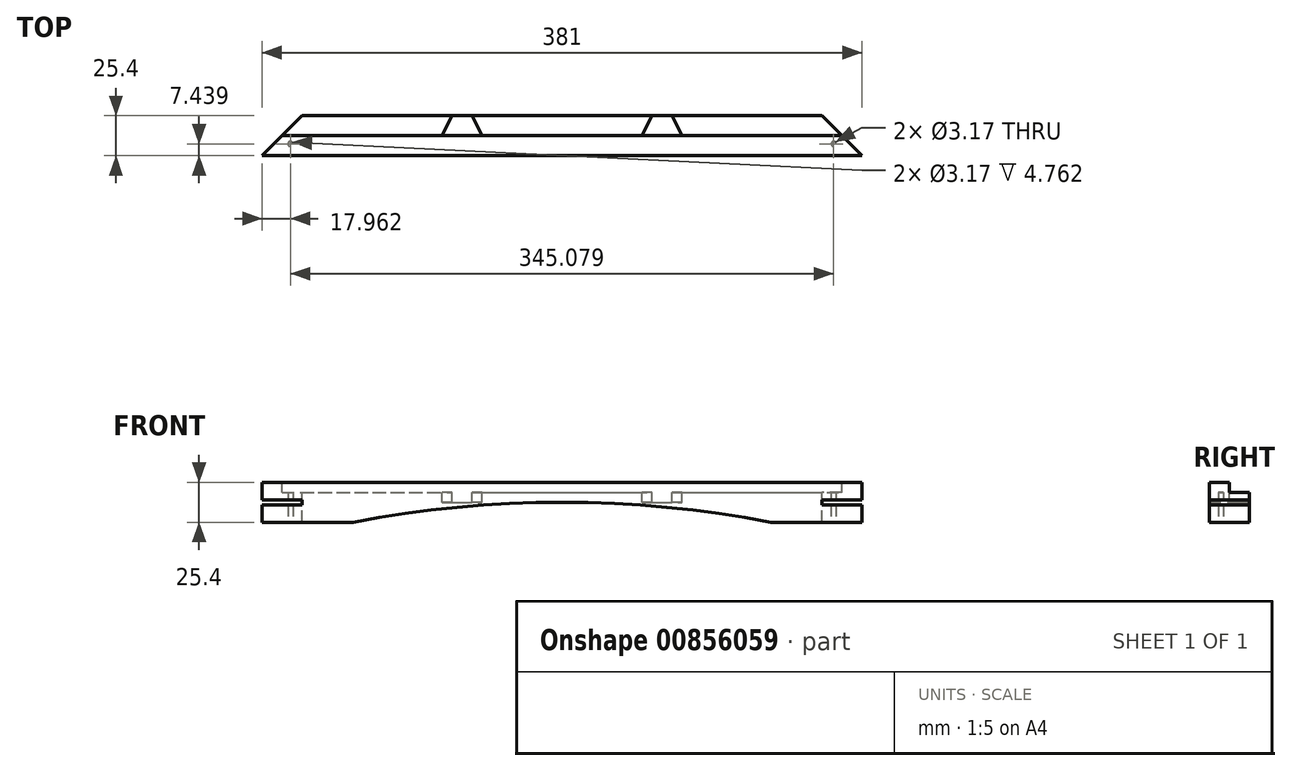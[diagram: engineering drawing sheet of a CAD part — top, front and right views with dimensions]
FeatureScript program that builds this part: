
annotation { "Feature Type Name" : "Feature", "Feature Type Description" : "" }
export const myFeature = defineFeature(function(context is Context, id is Id, definition is map)
    precondition{}
    {
        {
            var Q0;
            Q0=qCreatedBy(makeId("Front.planeOp"),FACE);
            var sketch = newSketch(context, id + "F0", { "sketchPlane" : qUnion([Q0])});
            skLineSegment(sketch, "E0.bottom", {"start": v(-134.34, 12.7) * mm, "end": v(246.66, 12.7) * mm});
            skLineSegment(sketch, "E0.top", {"start": v(-134.34, -12.7) * mm, "end": v(246.66, -12.7) * mm});
            skLineSegment(sketch, "E0.left", {"start": v(-134.34, 12.7) * mm, "end": v(-134.34, -12.7) * mm});
            skLineSegment(sketch, "E0.right", {"start": v(246.66, 12.7) * mm, "end": v(246.66, -12.7) * mm});
            skCircle(sketch, "E1", {"center": v(56.16, -698.5) * mm, "radius": 698.5 * mm});
            skLineSegment(sketch, "E2", {"start": v(-70.84, -12.7) * mm, "end": v(81.85, -12.7) * mm});
            skSolve(sketch);
        }
        {
            var Q0;
            Q0=makeQuery(id+"F0.imprint","IMPRINT",FACE,{"disambiguationData":[TD([[makeQuery(id+"F0.imprint","IMPRINT",EDGE,{"derivedFrom":sQuery(id+"F0.wireOp",EDGE,"E0.bottom")}),-1.0]])]});
            extrude(context, id + "F1", {"entities" : qUnion([Q0]), "depth" : 25.4 * mm, "offsetDistance" : 25.4 * mm});
        }
        {
            var Q0;
            Q0=makeQuery(id+"F1.opExtrude","SWEPT_FACE",FACE,{"disambiguationData":[OSD([sQuery(id+"F0.wireOp",EDGE,"E0.right")])]});
            var sketch = newSketch(context, id + "F2", { "sketchPlane" : qUnion([Q0])});
            skLineSegment(sketch, "E3.bottom", {"start": v(-25.4, 1.59) * mm, "end": v(0, 1.59) * mm});
            skLineSegment(sketch, "E3.top", {"start": v(-25.4, -1.59) * mm, "end": v(0, -1.59) * mm});
            skLineSegment(sketch, "E3.left", {"start": v(-25.4, 1.59) * mm, "end": v(-25.4, -1.59) * mm});
            skLineSegment(sketch, "E3.right", {"start": v(0, 1.59) * mm, "end": v(0, -1.59) * mm});
            skSolve(sketch);
        }
        {
            var Q0;
            Q0=makeQuery(id+"F2.imprint","IMPRINT",FACE,{"disambiguationData":[TD([[makeQuery(id+"F2.imprint","IMPRINT",EDGE,{"derivedFrom":sQuery(id+"F2.wireOp",EDGE,"E3.bottom")}),-1.0]])]});
            extrude(context, id + "F3", {"entities" : qUnion([Q0]), "operationType" : NewBodyOperationType.REMOVE, "oppositeDirection" : true, "depth" : 25.4 * mm, "offsetDistance" : 25.4 * mm});
        }
        {
            var Q0;
            Q0=makeQuery(id+"F1.opExtrude","SWEPT_FACE",FACE,{"disambiguationData":[OSD([sQuery(id+"F0.wireOp",EDGE,"E0.left")])]});
            var sketch = newSketch(context, id + "F4", { "sketchPlane" : qUnion([Q0])});
            skLineSegment(sketch, "E4.bottom", {"start": v(0, 1.59) * mm, "end": v(25.4, 1.59) * mm});
            skLineSegment(sketch, "E4.top", {"start": v(0, -1.59) * mm, "end": v(25.4, -1.59) * mm});
            skLineSegment(sketch, "E4.left", {"start": v(0, 1.59) * mm, "end": v(0, -1.59) * mm});
            skLineSegment(sketch, "E4.right", {"start": v(25.4, 1.59) * mm, "end": v(25.4, -1.59) * mm});
            skSolve(sketch);
        }
        {
            var Q0;
            Q0=makeQuery(id+"F4.imprint","IMPRINT",FACE,{"disambiguationData":[TD([[makeQuery(id+"F4.imprint","IMPRINT",EDGE,{"derivedFrom":sQuery(id+"F4.wireOp",EDGE,"E4.bottom")}),-1.0]])]});
            extrude(context, id + "F5", {"entities" : qUnion([Q0]), "operationType" : NewBodyOperationType.REMOVE, "oppositeDirection" : true, "depth" : 25.4 * mm, "offsetDistance" : 25.4 * mm});
        }
        {
            var Q0;
            Q0=makeQuery(id+"F1.opExtrude","SWEPT_FACE",FACE,{"disambiguationData":[OSD([sQuery(id+"F0.wireOp",EDGE,"E0.bottom")])]});
            var sketch = newSketch(context, id + "F6", { "sketchPlane" : qUnion([Q0])});
            skLineSegment(sketch, "E5", {"start": v(-134.34, -25.4) * mm, "end": v(-108.94, 0) * mm});
            skLineSegment(sketch, "E6", {"start": v(246.66, -25.4) * mm, "end": v(221.26, 0) * mm});
            skLineSegment(sketch, "E7", {"start": v(-121.64, -12.7) * mm, "end": v(233.96, -12.7) * mm});
            skSolve(sketch);
        }
        {
            var Q0;
            {var subQ0=sQuery(id+"F6.wireOp",EDGE,"E5");Q0=makeQuery(id+"F6.imprint","IMPRINT",FACE,{"disambiguationData":[TD([[makeQuery(id+"F6.imprint","IMPRINT",EDGE,{"derivedFrom":subQ0}),1.0]])]});}
            var Q1;
            {var subQ0=sQuery(id+"F6.wireOp",EDGE,"E6");Q1=makeQuery(id+"F6.imprint","IMPRINT",FACE,{"disambiguationData":[TD([[makeQuery(id+"F6.imprint","IMPRINT",EDGE,{"derivedFrom":subQ0}),-1.0]])]});}
            extrude(context, id + "F7", {"entities" : qUnion([Q0, Q1]), "operationType" : NewBodyOperationType.REMOVE, "oppositeDirection" : true, "depth" : 25.4 * mm, "offsetDistance" : 25.4 * mm});
        }
        {
            var Q0;
            {var subQ3=sQuery(id+"F6.wireOp",EDGE,"E7");Q0=makeQuery(id+"F6.imprint","IMPRINT",FACE,{"disambiguationData":[TD([[makeQuery(id+"F6.imprint","IMPRINT",EDGE,{"derivedFrom":subQ3}),1.0]])]});}
            extrude(context, id + "F8", {"entities" : qUnion([Q0]), "operationType" : NewBodyOperationType.REMOVE, "oppositeDirection" : true, "depth" : 6.35 * mm, "offsetDistance" : 25.4 * mm});
        }
        {
            var Q0;
            Q0=makeQuery(id+"F8.boolean.opBoolean","COPY",FACE,{"derivedFrom":makeQuery(id+"F8.opExtrude","CAP_FACE",FACE,{"disambiguationData":[OSD([sQuery(id+"F0.wireOp",EDGE,"E0.bottom"),sQuery(id+"F6.wireOp",EDGE,"E5"),sQuery(id+"F6.wireOp",EDGE,"E6"),sQuery(id+"F6.wireOp",EDGE,"E7")])],"isStart":false})});
            var sketch = newSketch(context, id + "F9", { "sketchPlane" : qUnion([Q0])});
            skLineSegment(sketch, "E8", {"start": v(-13.69, 0) * mm, "end": v(-20.04, -12.7) * mm});
            skLineSegment(sketch, "E9", {"start": v(-20.04, -12.7) * mm, "end": v(5.36, -12.7) * mm});
            skLineSegment(sketch, "E10", {"start": v(5.36, -12.7) * mm, "end": v(-0.99, 0) * mm});
            skLineSegment(sketch, "E11", {"start": v(113.31, 0) * mm, "end": v(106.96, -12.7) * mm});
            skLineSegment(sketch, "E12", {"start": v(106.96, -12.7) * mm, "end": v(132.36, -12.7) * mm});
            skLineSegment(sketch, "E13", {"start": v(132.36, -12.7) * mm, "end": v(126.01, 0) * mm});
            skLineSegment(sketch, "E14", {"start": v(-121.64, -12.7) * mm, "end": v(-20.04, -12.7) * mm});
            skLineSegment(sketch, "E15", {"start": v(5.36, -12.7) * mm, "end": v(106.96, -12.7) * mm});
            skLineSegment(sketch, "E16", {"start": v(132.36, -12.7) * mm, "end": v(233.96, -12.7) * mm});
            skLineSegment(sketch, "E17", {"start": v(-13.69, 0) * mm, "end": v(-108.94, 0) * mm});
            skLineSegment(sketch, "E18", {"start": v(-0.99, 0) * mm, "end": v(113.31, 0) * mm});
            skLineSegment(sketch, "E19", {"start": v(126.01, 0) * mm, "end": v(221.26, 0) * mm});
            skSolve(sketch);
        }
        {
            var Q0;
            {var subQ0=sQuery(id+"F9.wireOp",EDGE,"E8");Q0=makeQuery(id+"F9.imprint","IMPRINT",FACE,{"disambiguationData":[TD([[makeQuery(id+"F9.imprint","IMPRINT",EDGE,{"derivedFrom":subQ0}),1.0]])]});}
            var Q1;
            {var subQ0=sQuery(id+"F9.wireOp",EDGE,"E11");Q1=makeQuery(id+"F9.imprint","IMPRINT",FACE,{"disambiguationData":[TD([[makeQuery(id+"F9.imprint","IMPRINT",EDGE,{"derivedFrom":subQ0}),1.0]])]});}
            extrude(context, id + "F10", {"entities" : qUnion([Q0, Q1]), "operationType" : NewBodyOperationType.REMOVE, "oppositeDirection" : true, "depth" : 6.35 * mm, "offsetDistance" : 25.4 * mm});
        }
        {
            var Q0;
            {var subQ0=sQuery(id+"F0.wireOp",EDGE,"E0.top");Q0=makeQuery(id+"F1.opExtrude","SWEPT_FACE",FACE,{"disambiguationData":[OSD([subQ0]),TDD([makeQuery(id+"F0.imprint","IMPRINT",EDGE,{"disambiguationData":[TD([[makeQuery(id+"F0.imprint","INTERSECT",VERTEX,{"derivedFrom":[subQ0,sQuery(id+"F0.wireOp",EDGE,"E0.left")]}),-1.0]])],"derivedFrom":subQ0})])]});}
            var sketch = newSketch(context, id + "F11", { "sketchPlane" : qUnion([Q0])});
            skLineSegment(sketch, "E20", {"start": v(-108.94, 0) * mm, "end": v(-108.94, 25.4) * mm});
            skCircle(sketch, "E21", {"center": v(-116.38, 17.96) * mm, "radius": 1.59 * mm});
            skLineSegment(sketch, "E22", {"start": v(-116.38, 17.96) * mm, "end": v(-116.38, 25.4) * mm});
            skLineSegment(sketch, "E23", {"start": v(-116.38, 17.96) * mm, "end": v(-108.94, 17.96) * mm});
            skLineSegment(sketch, "E24", {"start": v(-116.38, 17.96) * mm, "end": v(-121.64, 12.7) * mm});
            skPoint(sketch, "E24.endSnap0", {"position": v(-121.64, 12.7) * mm});
            skSolve(sketch);
        }
        {
            var Q0;
            {var subQ0=sQuery(id+"F0.wireOp",EDGE,"E0.top");Q0=makeQuery(id+"F1.opExtrude","SWEPT_FACE",FACE,{"disambiguationData":[OSD([subQ0]),TDD([makeQuery(id+"F0.imprint","IMPRINT",EDGE,{"disambiguationData":[TD([[makeQuery(id+"F0.imprint","INTERSECT",VERTEX,{"derivedFrom":[subQ0,sQuery(id+"F0.wireOp",EDGE,"E0.right")]}),1.0]])],"derivedFrom":subQ0})])]});}
            var sketch = newSketch(context, id + "F12", { "sketchPlane" : qUnion([Q0])});
            skLineSegment(sketch, "E25", {"start": v(221.26, 0) * mm, "end": v(221.26, 25.4) * mm});
            skCircle(sketch, "E26", {"center": v(228.7, 17.96) * mm, "radius": 1.59 * mm});
            skLineSegment(sketch, "E27", {"start": v(228.7, 17.96) * mm, "end": v(221.26, 17.96) * mm});
            skLineSegment(sketch, "E28", {"start": v(228.7, 17.96) * mm, "end": v(228.7, 25.4) * mm});
            skLineSegment(sketch, "E29", {"start": v(228.7, 17.96) * mm, "end": v(233.96, 12.7) * mm});
            skSolve(sketch);
        }
        {
            var Q0;
            {var subQ0=sQuery(id+"F11.wireOp",EDGE,"E22");var subQ1=sQuery(id+"F11.wireOp",EDGE,"E21");var subQ2=makeQuery(id+"F11.imprint","INTERSECT",VERTEX,{"derivedFrom":[subQ1,subQ0]});Q0=makeQuery(id+"F11.imprint","IMPRINT",FACE,{"disambiguationData":[TD([[makeQuery(id+"F11.imprint","IMPRINT",EDGE,{"disambiguationData":[TD([[subQ2,-1.0]])],"derivedFrom":subQ1}),1.0]])]});}
            var Q1;
            {var subQ0=sQuery(id+"F11.wireOp",EDGE,"E22");var subQ1=sQuery(id+"F11.wireOp",EDGE,"E21");var subQ2=makeQuery(id+"F11.imprint","INTERSECT",VERTEX,{"derivedFrom":[subQ1,subQ0]});Q1=makeQuery(id+"F11.imprint","IMPRINT",FACE,{"disambiguationData":[TD([[makeQuery(id+"F11.imprint","IMPRINT",EDGE,{"disambiguationData":[TD([[subQ2,1.0]])],"derivedFrom":subQ1}),1.0]])]});}
            var Q2;
            {var subQ0=sQuery(id+"F11.wireOp",EDGE,"E23");var subQ1=sQuery(id+"F11.wireOp",EDGE,"E21");var subQ2=makeQuery(id+"F11.imprint","INTERSECT",VERTEX,{"derivedFrom":[subQ1,subQ0]});Q2=makeQuery(id+"F11.imprint","IMPRINT",FACE,{"disambiguationData":[TD([[makeQuery(id+"F11.imprint","IMPRINT",EDGE,{"disambiguationData":[TD([[subQ2,1.0]])],"derivedFrom":subQ1}),1.0]])]});}
            var Q3;
            {var subQ0=sQuery(id+"F12.wireOp",EDGE,"E28");var subQ1=sQuery(id+"F12.wireOp",EDGE,"E26");var subQ2=makeQuery(id+"F12.imprint","INTERSECT",VERTEX,{"derivedFrom":[subQ1,subQ0]});Q3=makeQuery(id+"F12.imprint","IMPRINT",FACE,{"disambiguationData":[TD([[makeQuery(id+"F12.imprint","IMPRINT",EDGE,{"disambiguationData":[TD([[subQ2,1.0]])],"derivedFrom":subQ1}),1.0]])]});}
            var Q4;
            {var subQ0=sQuery(id+"F12.wireOp",EDGE,"E27");var subQ1=sQuery(id+"F12.wireOp",EDGE,"E26");var subQ2=makeQuery(id+"F12.imprint","INTERSECT",VERTEX,{"derivedFrom":[subQ1,subQ0]});Q4=makeQuery(id+"F12.imprint","IMPRINT",FACE,{"disambiguationData":[TD([[makeQuery(id+"F12.imprint","IMPRINT",EDGE,{"disambiguationData":[TD([[subQ2,1.0]])],"derivedFrom":subQ1}),1.0]])]});}
            var Q5;
            {var subQ0=sQuery(id+"F12.wireOp",EDGE,"E27");var subQ1=sQuery(id+"F12.wireOp",EDGE,"E26");var subQ2=makeQuery(id+"F12.imprint","INTERSECT",VERTEX,{"derivedFrom":[subQ1,subQ0]});Q5=makeQuery(id+"F12.imprint","IMPRINT",FACE,{"disambiguationData":[TD([[makeQuery(id+"F12.imprint","IMPRINT",EDGE,{"disambiguationData":[TD([[subQ2,-1.0]])],"derivedFrom":subQ1}),1.0]])]});}
            extrude(context, id + "F13", {"entities" : qUnion([Q0, Q1, Q2, Q3, Q4, Q5]), "operationType" : NewBodyOperationType.REMOVE, "oppositeDirection" : true, "depth" : 19.05 * mm, "offsetDistance" : 25.4 * mm});
        }
    });
